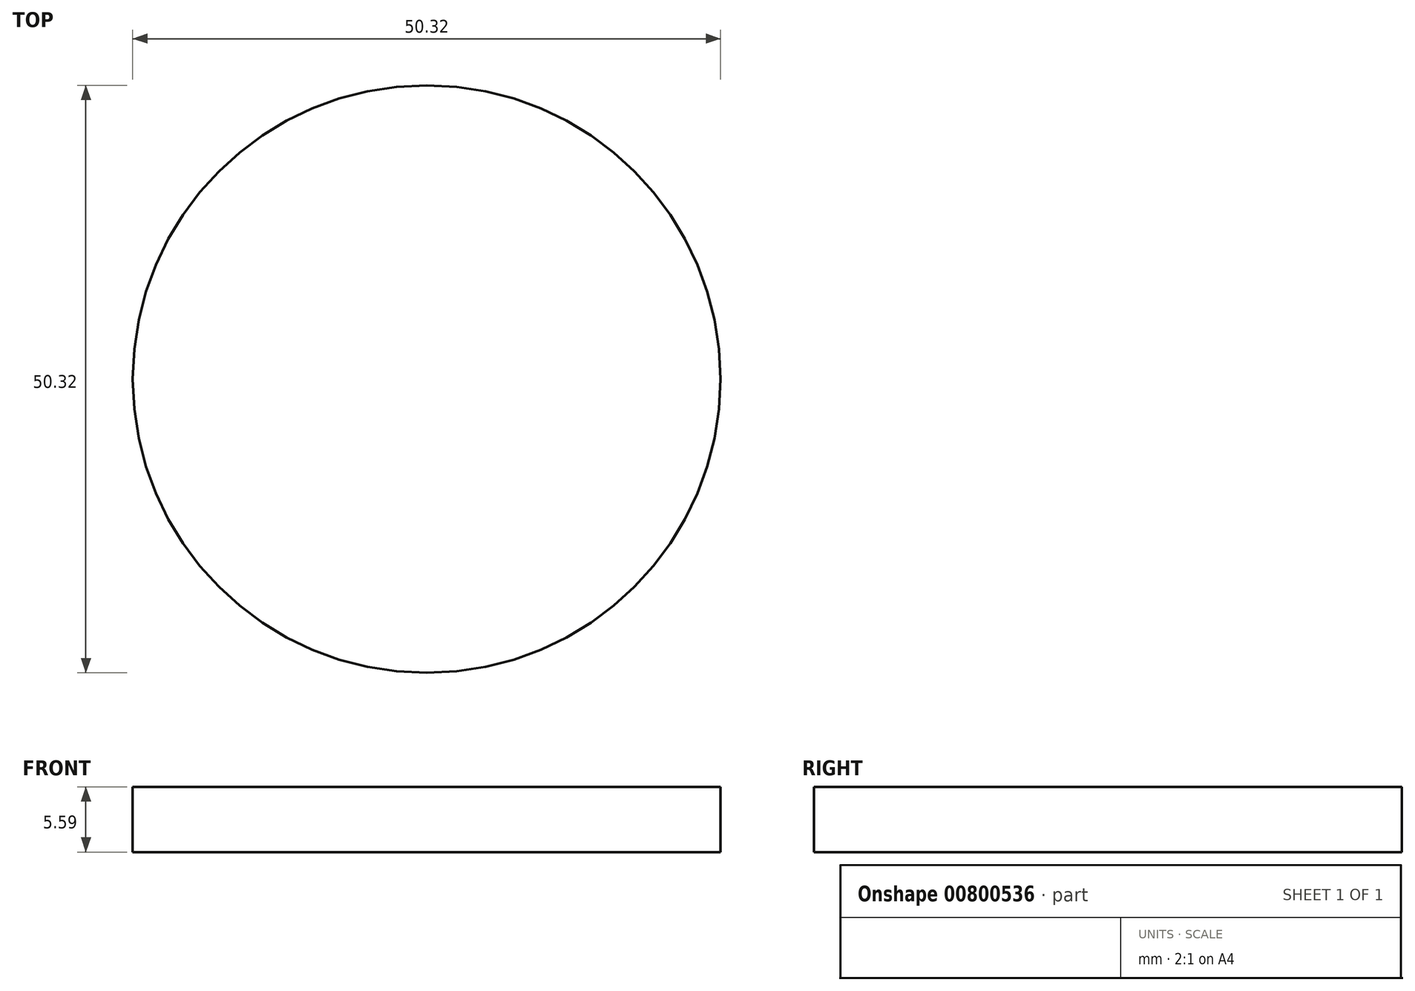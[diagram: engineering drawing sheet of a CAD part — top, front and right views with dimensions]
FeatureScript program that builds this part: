
annotation { "Feature Type Name" : "Feature", "Feature Type Description" : "" }
export const myFeature = defineFeature(function(context is Context, id is Id, definition is map)
    precondition{}
    {
        {
            var Q0;
            Q0=qCreatedBy(makeId("Top.planeOp"),FACE);
            var sketch = newSketch(context, id + "F0", { "sketchPlane" : qUnion([Q0])});
            skCircle(sketch, "E0", {"center": v(0, 0) * mm, "radius": 25.16 * mm});
            skSolve(sketch);
        }
        {
            var Q0;
            Q0=makeQuery(id+"F0.imprint","IMPRINT",FACE,{"disambiguationData":[TD([[makeQuery(id+"F0.imprint","IMPRINT",EDGE,{"derivedFrom":sQuery(id+"F0.wireOp",EDGE,"E0")}),1.0]])]});
            extrude(context, id + "F1", {"entities" : qUnion([Q0]), "depth" : 5.6 * mm, "offsetDistance" : 25.4 * mm});
        }
    });
